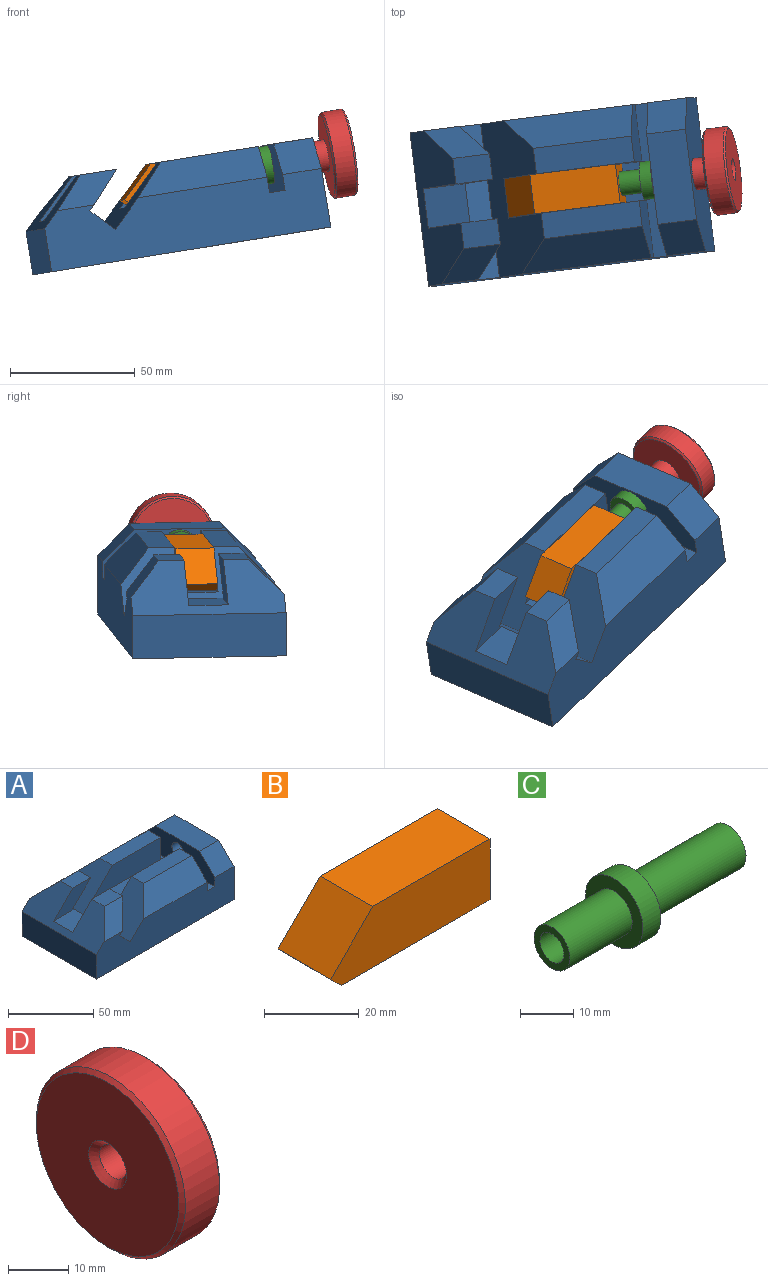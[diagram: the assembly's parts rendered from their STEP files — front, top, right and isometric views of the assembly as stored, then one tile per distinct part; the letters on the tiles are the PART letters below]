
ASSEMBLY  parts=4 mates=3
PART A: 31 faces, bbox 114.3x61.9x36.5 mm
  f0: plane 40.08x10.31mm, normal (0,0,1), area 413.3mm2, adj f2,f3,f22,f26
  f1: plane 14.99x10.31mm, normal (0,0,1), area 154.5mm2, adj f5,f20,f24,f28
  f2: plane 61.93x19.05mm, normal (1,0,0), area 766mm2, adj f0,f11,f12,f15,f16,f21,f22,f23
  f3: plane 61.93x23.83mm, normal (-0.71,0,0.71), area 1501.4mm2, adj f0,f4,f12,f15,f16,f21,f22,f23
  f4: plane 61.93x8.98mm, normal (0.71,0,0.71), area 763.3mm2, adj f3,f5,f6,f15,f16,f18,f19,f20
  f5: plane 23.01x14.85mm, normal (0.71,0,-0.71), area 369.1mm2, adj f1,f4,f16,f20,f28
  f6: plane 23.01x14.85mm, normal (0.71,0,-0.71), area 369.1mm2, adj f4,f13,f15,f19,f27
  f7: plane 61.93x17.48mm, normal (-1,0,0), area 1082.2mm2, adj f14,f15,f16,f24
  f8: plane 61.93x36.53mm, normal (1,0,0), area 2029.3mm2, adj f9,f14,f15,f16,f17,f25,f30
  f9: plane 36.53x15.88mm, normal (0,0,1), area 579.8mm2, adj f8,f10,f25,f30
  f10: plane 61.93x19.05mm, normal (-1,0,0), area 947.1mm2, adj f9,f11,f15,f16,f17,f25,f30
  f11: plane 61.93x6.35mm, normal (0,0,1), area 393.2mm2, adj f2,f10,f15,f16
  f12: plane 40.08x10.31mm, normal (0,0,1), area 413.3mm2, adj f2,f3,f21,f29
  f13: plane 14.99x10.31mm, normal (0,0,1), area 154.5mm2, adj f6,f19,f24,f27
  f14: plane 114.3x61.93mm, normal (0,0,-1), area 7078.1mm2, adj f7,f8,f15,f16
  f15: plane 114.3x23.83mm, normal (0,1,0), area 2543.6mm2, adj f2,f3,f4,f6,f7,f8,f10,f11
  f16: plane 114.3x23.83mm, normal (0,-1,0), area 2543.6mm2, adj f2,f3,f4,f5,f7,f8,f10,f11
  f17: cylinder r=4.76mm len=15.88mm, axis (1,0,0), area 475mm2, adj f8,f10
  f18: plane 17.05x15.9mm, normal (0,0,1), area 271mm2, adj f4,f19,f20,f24
  f19: plane 30.86x15.88mm, normal (0,-1,0), area 239mm2, adj f4,f6,f13,f18,f24
  f20: plane 30.86x15.88mm, normal (0,1,0), area 239mm2, adj f1,f4,f5,f18,f24
  f21: plane 55.95x15.88mm, normal (0,1,0), area 762.3mm2, adj f2,f3,f12,f23
  f22: plane 55.95x15.88mm, normal (0,-1,0), area 762.3mm2, adj f0,f2,f3,f23
  f23: plane 55.95x15.9mm, normal (0,0,1), area 889.7mm2, adj f2,f3,f21,f22
  f24: plane 61.93x19.05mm, normal (-0.71,0,0.71), area 1083.2mm2, adj f1,f7,f13,f15,f16,f18,f19,f20
  f25: plane 15.88x12.7mm, normal (0,0.71,0.71), area 285.1mm2, adj f8,f9,f10,f15
  f26: plane 52.78x12.7mm, normal (0,0.71,0.71), area 833.9mm2, adj f0,f2,f3,f15
  f27: plane 27.69x12.7mm, normal (0,0.71,0.71), area 269.2mm2, adj f6,f13,f15,f24
  f28: plane 27.69x12.7mm, normal (0,-0.71,0.71), area 269.2mm2, adj f1,f5,f16,f24
  f29: plane 52.78x12.7mm, normal (0,-0.71,0.71), area 833.9mm2, adj f2,f3,f12,f16
  f30: plane 15.88x12.7mm, normal (0,-0.71,0.71), area 285.1mm2, adj f8,f9,f10,f16
PART B: 9 faces, bbox 47.6x15.7x15.7 mm
  f0: plane 15.75x3.18mm, normal (-0.71,0,-0.71), area 70.7mm2, adj f1,f4,f5,f6
  f1: plane 44.45x15.75mm, normal (0,0,-1), area 700mm2, adj f0,f2,f5,f6
  f2: plane 15.75x15.75mm, normal (1,0,0), area 176.7mm2, adj f1,f3,f5,f6,f7
  f3: plane 35.05x15.75mm, normal (0,0,1), area 552mm2, adj f2,f4,f5,f6
  f4: plane 15.75x12.57mm, normal (-0.71,0,0.71), area 280mm2, adj f0,f3,f5,f6
  f5: plane 47.63x15.75mm, normal (0,1,0), area 665.9mm2, adj f0,f1,f2,f3,f4
  f6: plane 47.63x15.75mm, normal (0,-1,0), area 665.9mm2, adj f0,f1,f2,f3,f4
  f7: cylinder r=4.76mm len=25.4mm, axis (1,0,0), area 760.1mm2, adj f2,f8
  f8: plane 9.53x9.53mm, normal (1,0,0), area 71.3mm2, adj f7
PART C: 9 faces, bbox 46.7x15.2x15.2 mm
  f0: cylinder r=4.76mm len=16.51mm, axis (-1,0,0), area 494mm2, adj f1,f4
  f1: plane 9.53x9.53mm, normal (-1,0,0), area 39.6mm2, adj f0,f7
  f2: cylinder r=7.62mm len=15.24mm, axis (-1,0,0), area 228.6mm2, adj f3,f4
  f3: plane 15.24x15.24mm, normal (1,0,0), area 111.2mm2, adj f2,f5
  f4: plane 15.24x15.24mm, normal (-1,0,0), area 111.2mm2, adj f0,f2
  f5: cylinder r=4.76mm len=25.4mm, axis (-1,0,0), area 760.1mm2, adj f3,f6
  f6: plane 9.53x9.53mm, normal (1,0,0), area 71.3mm2, adj f5
  f7: cylinder r=3.17mm len=12.7mm, axis (-1,0,0), area 253.4mm2, adj f1,f8
  f8: plane 6.35x6.35mm, normal (-1,0,0), area 31.7mm2, adj f7
PART D: 9 faces, bbox 15.9x34.9x34.9 mm
  f0: cylinder r=17.46mm len=34.93mm, axis (1,0,0), area 877.9mm2, adj f7,f8
  f1: plane 33.4x33.4mm, normal (-1,0,0), area 814.1mm2, adj f6,f8
  f2: plane 33.4x33.4mm, normal (1,0,0), area 749.5mm2, adj f3,f7
  f3: cylinder r=6.35mm len=12.7mm, axis (-1,0,0), area 253.4mm2, adj f2,f4
  f4: plane 12.7x12.7mm, normal (1,0,0), area 95mm2, adj f3,f5
  f5: cylinder r=3.17mm len=14.61mm, axis (1,0,0), area 291.4mm2, adj f4,f6
  f6: cone r=4.45mm half-angle=45deg, axis (-1,0,0), area 43mm2, adj f1,f5
  f7: cone r=16.7mm half-angle=45deg, axis (-1,0,0), area 115.7mm2, adj f0,f2
  f8: cone r=17.46mm half-angle=45deg, axis (1,0,0), area 115.7mm2, adj f0,f1
PLACE A rot(axis=(-0.05,-0.79,0.61),11.5deg) t=(-30.06,-34,-72.84)mm
PLACE B rot(axis=(-0.05,-0.79,0.61),11.5deg) t=(-0.21,-6.58,-47.09)mm
PLACE C rot(axis=(0.08,0,-1),173deg) t=(73.97,10.8,-27.2)mm
PLACE D rot(axis=(0.08,0,-1),173deg) t=(80.19,11.58,-26.21)mm
MATE revolute D.f5 <-> C.f7  axis (-0.98,-0.12,-0.16) through (73.97,10.8,-27.2)mm
MATE slider B.f7 <-> C.f5  axis (0.98,0.12,0.16) through (31.81,5.52,-33.97)mm
MATE revolute C.f0 <-> A.f17  axis (0.98,0.12,0.16) through (65.88,9.79,-28.5)mm
